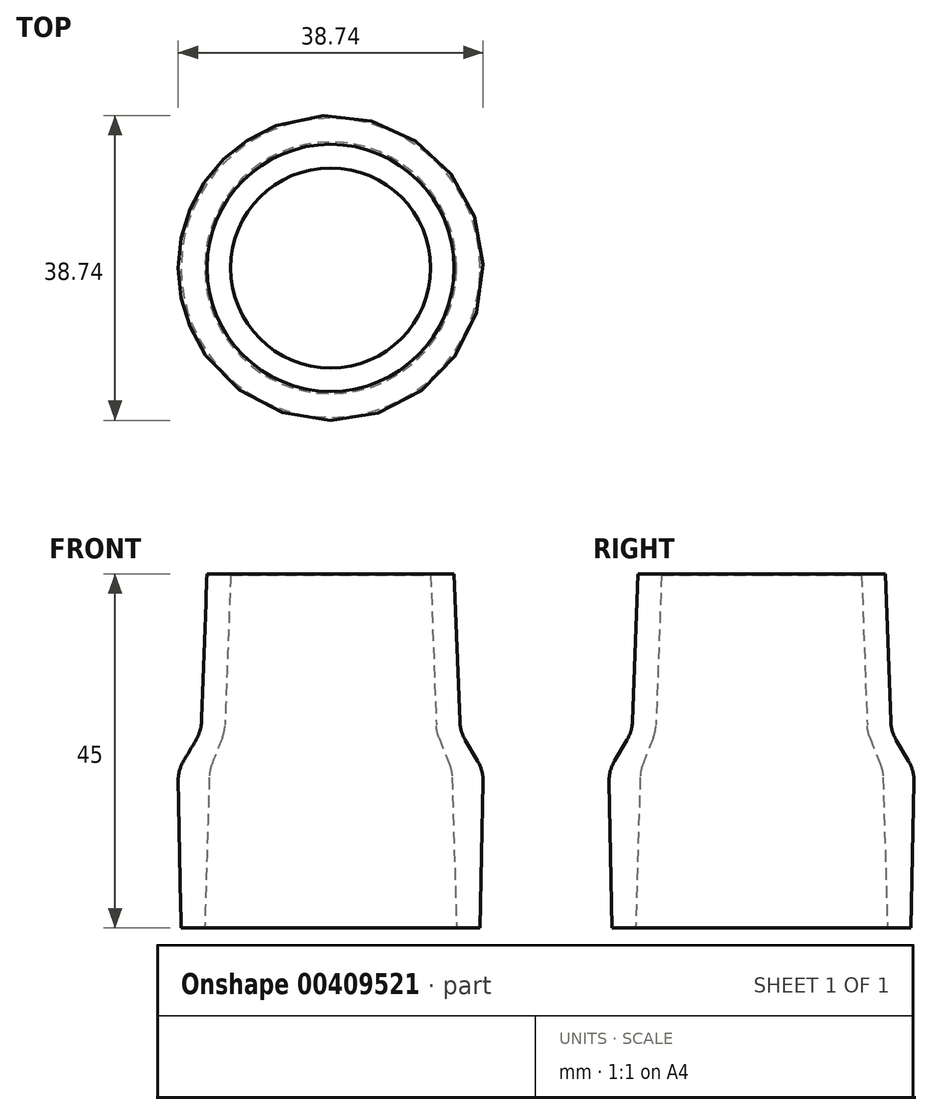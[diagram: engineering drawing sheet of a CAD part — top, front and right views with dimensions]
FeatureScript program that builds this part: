
annotation { "Feature Type Name" : "Feature", "Feature Type Description" : "" }
export const myFeature = defineFeature(function(context is Context, id is Id, definition is map)
    precondition{}
    {
        {
            var Q0;
            Q0=qCreatedBy(makeId("Front.planeOp"),FACE);
            var sketch = newSketch(context, id + "F0", { "sketchPlane" : qUnion([Q0])});
            skLineSegment(sketch, "E0", {"start": v(16, 0) * mm, "end": v(15.43, 19.13) * mm});
            skLineSegment(sketch, "E1", {"start": v(19, 0) * mm, "end": v(19.37, 18.58) * mm});
            skLineSegment(sketch, "E2", {"start": v(16.4, 26.26) * mm, "end": v(15.7, 45) * mm});
            skLineSegment(sketch, "E3.0", {"start": v(13.42, 25.83) * mm, "end": v(12.7, 44.85) * mm});
            skLineSegment(sketch, "E4", {"start": v(12.7, 44.85) * mm, "end": v(15.7, 45) * mm});
            skLineSegment(sketch, "E5", {"start": v(17.1, 23.91) * mm, "end": v(18.68, 21.22) * mm});
            skLineSegment(sketch, "E6", {"start": v(13.76, 24.2) * mm, "end": v(15.08, 20.8) * mm});
            skLineSegment(sketch, "E7", {"start": v(16, 0) * mm, "end": v(19, 0) * mm});
            skPoint(sketch, "E8.visualSharp", {"position": v(13.45, 24.99) * mm});
            skArc(sketch, "E8.filletArc", {"start": v(13.42, 25.83) * mm, "mid": v(13.52, 25) * mm, "end": v(13.76, 24.2) * mm});
            skPoint(sketch, "E9.visualSharp", {"position": v(16.45, 25) * mm});
            skArc(sketch, "E9.filletArc", {"start": v(16.4, 26.26) * mm, "mid": v(16.6, 25.04) * mm, "end": v(17.1, 23.91) * mm});
            skPoint(sketch, "E10.visualSharp", {"position": v(19.4, 20) * mm});
            skArc(sketch, "E10.filletArc", {"start": v(19.37, 18.58) * mm, "mid": v(19.2, 19.95) * mm, "end": v(18.68, 21.22) * mm});
            skPoint(sketch, "E11.visualSharp", {"position": v(15.4, 20) * mm});
            skArc(sketch, "E11.filletArc", {"start": v(15.43, 19.13) * mm, "mid": v(15.33, 19.99) * mm, "end": v(15.08, 20.8) * mm});
            skLineSegment(sketch, "E12", {"start": v(0, 0) * mm, "end": v(0, 44.85) * mm, "construction": true});
            skSolve(sketch);
        }
        {
            var Q0;
            Q0=makeQuery(id+"F0.imprint","IMPRINT",FACE,{"disambiguationData":[TD([[makeQuery(id+"F0.imprint","IMPRINT",EDGE,{"derivedFrom":sQuery(id+"F0.wireOp",EDGE,"E0")}),-1.0]])]});
            var Q1;
            Q1=sQuery(id+"F0.wireOp",EDGE,"E12");
            revolve(context, id + "F1", {"entities" : qUnion([Q0]), "axis" : qUnion([Q1]), "revolveType" : RevolveType.FULL});
        }
    });
